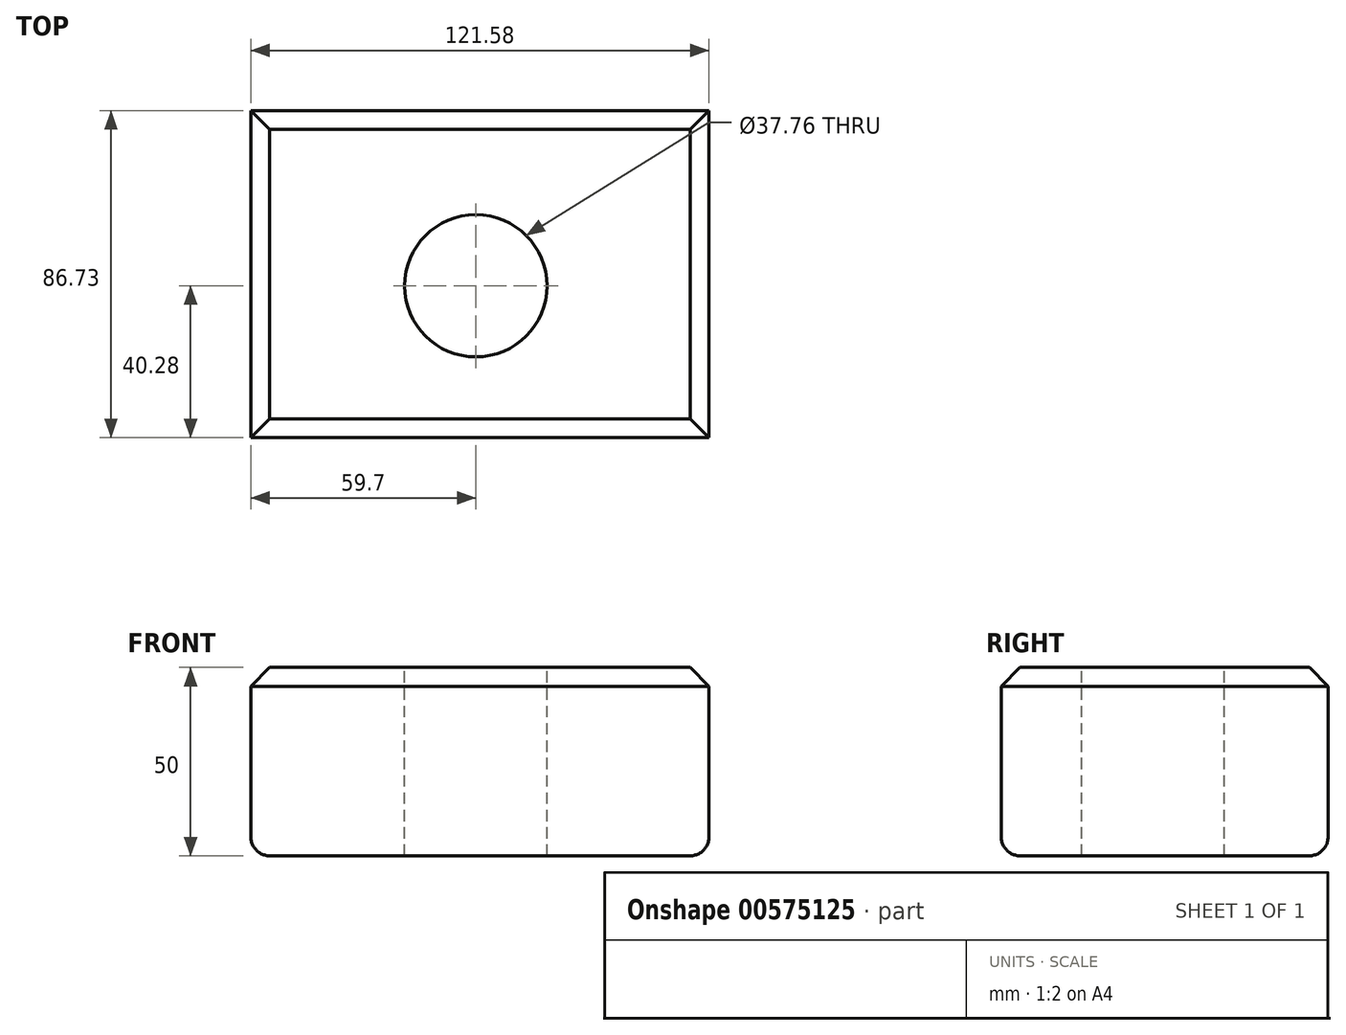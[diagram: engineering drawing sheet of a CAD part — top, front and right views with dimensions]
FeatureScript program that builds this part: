
annotation { "Feature Type Name" : "Feature", "Feature Type Description" : "" }
export const myFeature = defineFeature(function(context is Context, id is Id, definition is map)
    precondition{}
    {
        {
            var Q0;
            Q0=qCreatedBy(makeId("Top.planeOp"),FACE);
            var sketch = newSketch(context, id + "F0", { "sketchPlane" : qUnion([Q0])});
            skLineSegment(sketch, "E0.bottom", {"start": v(-59.7, 46.45) * mm, "end": v(61.88, 46.45) * mm});
            skLineSegment(sketch, "E0.top", {"start": v(-59.7, -40.28) * mm, "end": v(61.88, -40.28) * mm});
            skLineSegment(sketch, "E0.left", {"start": v(-59.7, 46.45) * mm, "end": v(-59.7, -40.28) * mm});
            skLineSegment(sketch, "E0.right", {"start": v(61.88, 46.45) * mm, "end": v(61.88, -40.28) * mm});
            skSolve(sketch);
        }
        {
            var Q0;
            Q0=makeQuery(id+"F0.imprint","IMPRINT",FACE,{"disambiguationData":[TD([[makeQuery(id+"F0.imprint","IMPRINT",EDGE,{"derivedFrom":sQuery(id+"F0.wireOp",EDGE,"E0.bottom")}),-1.0]])]});
            extrude(context, id + "F1", {"entities" : qUnion([Q0]), "depth" : 50 * mm, "offsetDistance" : 25 * mm});
        }
        {
            var Q0;
            Q0=makeQuery(id+"F1.opExtrude","CAP_FACE",FACE,{"disambiguationData":[OSD([sQuery(id+"F0.wireOp",EDGE,"E0.bottom"),sQuery(id+"F0.wireOp",EDGE,"E0.top"),sQuery(id+"F0.wireOp",EDGE,"E0.left"),sQuery(id+"F0.wireOp",EDGE,"E0.right")])],"isStart":false});
            var sketch = newSketch(context, id + "F2", { "sketchPlane" : qUnion([Q0])});
            skCircle(sketch, "E1", {"center": v(0, 0) * mm, "radius": 18.88 * mm});
            skSolve(sketch);
        }
        {
            var Q0;
            Q0=makeQuery(id+"F2.imprint","IMPRINT",FACE,{"disambiguationData":[TD([[makeQuery(id+"F2.imprint","IMPRINT",EDGE,{"derivedFrom":sQuery(id+"F2.wireOp",EDGE,"E1")}),1.0]])]});
            extrude(context, id + "F3", {"entities" : qUnion([Q0]), "operationType" : NewBodyOperationType.REMOVE, "oppositeDirection" : true, "depth" : 50 * mm, "offsetDistance" : 25 * mm});
        }
        {
            var Q0;
            Q0=makeQuery(id+"F1.opExtrude","CAP_EDGE",EDGE,{"disambiguationData":[OSD([sQuery(id+"F0.wireOp",EDGE,"E0.top")])],"isStart":false});
            var Q1;
            Q1=makeQuery(id+"F1.opExtrude","CAP_EDGE",EDGE,{"disambiguationData":[OSD([sQuery(id+"F0.wireOp",EDGE,"E0.right")])],"isStart":false});
            var Q2;
            Q2=makeQuery(id+"F1.opExtrude","CAP_EDGE",EDGE,{"disambiguationData":[OSD([sQuery(id+"F0.wireOp",EDGE,"E0.bottom")])],"isStart":false});
            var Q3;
            Q3=makeQuery(id+"F1.opExtrude","CAP_EDGE",EDGE,{"disambiguationData":[OSD([sQuery(id+"F0.wireOp",EDGE,"E0.left")])],"isStart":false});
            chamfer(context, id + "F4", {"entities" : qUnion([Q0, Q1, Q2, Q3]), "width" : 5 * mm, "tangentPropagation" : true});
        }
        {
            var Q0;
            Q0=makeQuery(id+"F1.opExtrude","CAP_EDGE",EDGE,{"disambiguationData":[OSD([sQuery(id+"F0.wireOp",EDGE,"E0.right")])],"isStart":true});
            var Q1;
            Q1=makeQuery(id+"F1.opExtrude","CAP_EDGE",EDGE,{"disambiguationData":[OSD([sQuery(id+"F0.wireOp",EDGE,"E0.top")])],"isStart":true});
            var Q2;
            Q2=makeQuery(id+"F1.opExtrude","CAP_EDGE",EDGE,{"disambiguationData":[OSD([sQuery(id+"F0.wireOp",EDGE,"E0.left")])],"isStart":true});
            var Q3;
            Q3=makeQuery(id+"F1.opExtrude","CAP_EDGE",EDGE,{"disambiguationData":[OSD([sQuery(id+"F0.wireOp",EDGE,"E0.bottom")])],"isStart":true});
            fillet(context, id + "F5", {"entities" : qUnion([Q0, Q1, Q2, Q3]), "radius" : 5 * mm, "tangentPropagation" : true, "allowEdgeOverflow" : false});
        }
    });
